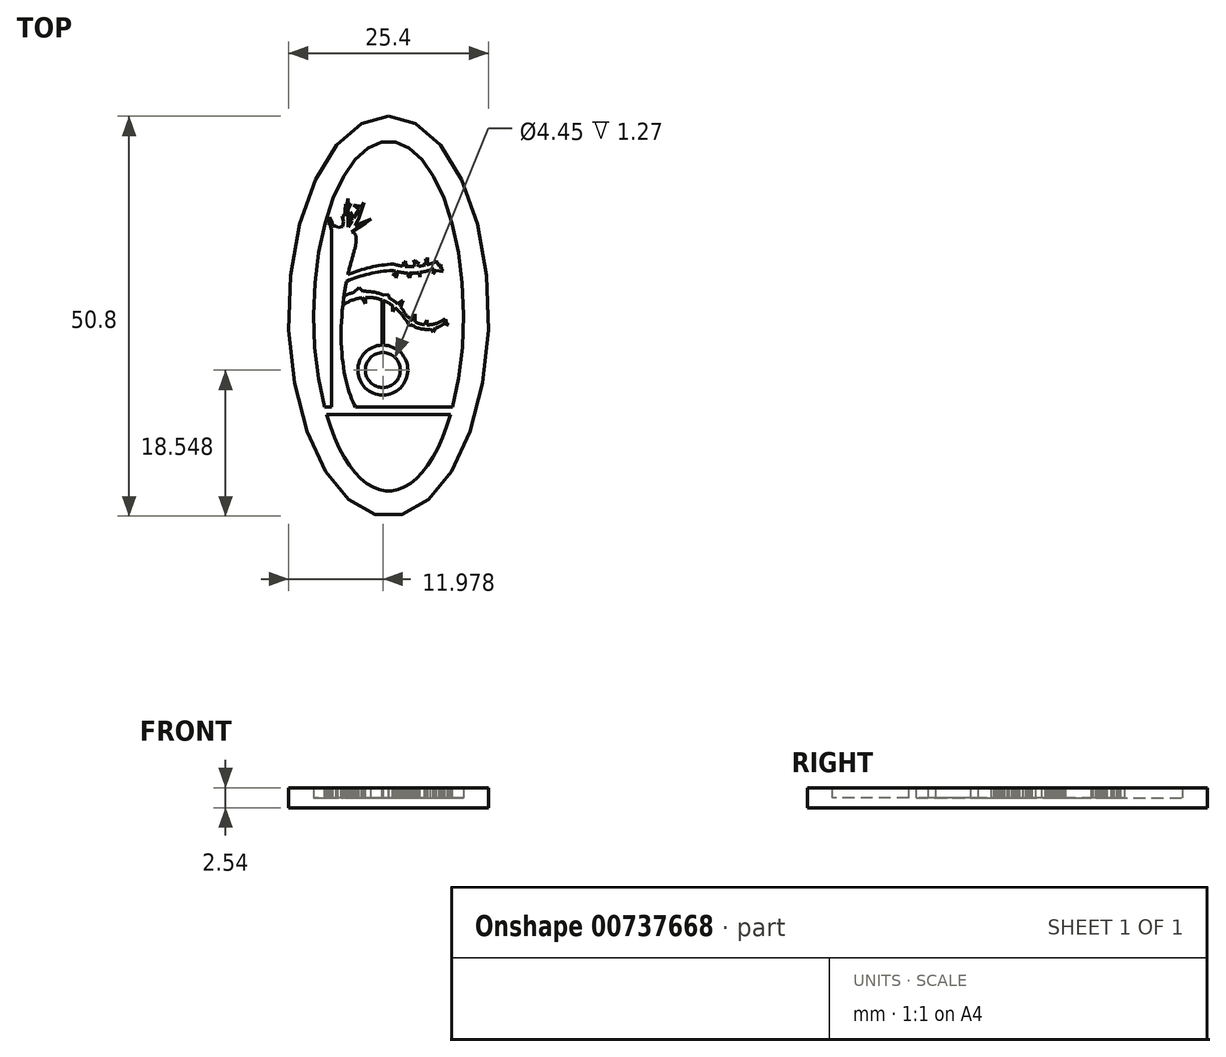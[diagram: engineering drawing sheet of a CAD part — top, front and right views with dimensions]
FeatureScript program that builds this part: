
annotation { "Feature Type Name" : "Feature", "Feature Type Description" : "" }
export const myFeature = defineFeature(function(context is Context, id is Id, definition is map)
    precondition{}
    {
        {
            var Q0;
            Q0=qCreatedBy(makeId("Top.planeOp"),FACE);
            var sketch = newSketch(context, id + "F0", { "sketchPlane" : qUnion([Q0])});
            skEllipse(sketch, "E0", {"center": v(0, 0) * mm, "majorRadius": 25.4 * mm, "minorRadius": 12.7 * mm, "majorAxis": v(0, 1)});
            skSolve(sketch);
        }
        {
            var Q0;
            Q0=qSketchRegion(id+"F0",true);
            extrude(context, id + "F1", {"entities" : qUnion([Q0]), "depth" : 2.54 * mm, "offsetDistance" : 25.4 * mm});
        }
        {
            var Q0;
            Q0=makeQuery(id+"F1.opExtrude","CAP_FACE",FACE,{"disambiguationData":[OSD([sQuery(id+"F0.wireOp",EDGE,"E0")])],"isStart":false});
            var sketch = newSketch(context, id + "F2", { "sketchPlane" : qUnion([Q0])});
            skEllipse(sketch, "E1", {"center": v(0, 0) * mm, "majorRadius": 22.23 * mm, "minorRadius": 9.53 * mm, "majorAxis": v(0, 1)});
            skSolve(sketch);
        }
        {
            var Q0;
            Q0=qSketchRegion(id+"F2",true);
            extrude(context, id + "F3", {"entities" : qUnion([Q0]), "operationType" : NewBodyOperationType.REMOVE, "oppositeDirection" : true, "depth" : 1.27 * mm, "offsetDistance" : 25.4 * mm});
        }
        {
            var Q0;
            Q0=makeQuery(id+"F2.imprint","IMPRINT",FACE,{"disambiguationData":[TD([[makeQuery(id+"F2.imprint","IMPRINT",EDGE,{"derivedFrom":sQuery(id+"F2.wireOp",EDGE,"E1")}),1.0]])]});
            var sketch = newSketch(context, id + "F4", { "sketchPlane" : qUnion([Q0])});
            skLineSegment(sketch, "E2", {"start": v(-7.24, 10.97) * mm, "end": v(-7.24, -11.57) * mm});
            skLineSegment(sketch, "E3", {"start": v(-7.24, -11.57) * mm, "end": v(-4.19, -11.57) * mm});
            skFitSpline(sketch, "E4", {"points": [v(-4.19, -11.57) * mm, v(-5.86, -5.45) * mm, v(-5, 5.96) * mm, v(-4.49, 10.63) * mm, v(-7.24, 10.97) * mm], "startDerivative": vector(-8.15, 15.39) * mm, "endDerivative": vector(-7.13, 8.4) * mm});
            skArc(sketch, "E5", {"start": v(0.52, 5.8) * mm, "mid": v(-2.54, 5.35) * mm, "end": v(-5.48, 4.37) * mm});
            skArc(sketch, "E6", {"start": v(0.52, 5.8) * mm, "mid": v(3.17, 5.47) * mm, "end": v(5.77, 6.03) * mm});
            skArc(sketch, "E7", {"start": v(1.81, 0.02) * mm, "mid": v(-1.7, 2.3) * mm, "end": v(-5.8, 1.4) * mm});
            skArc(sketch, "E8", {"start": v(1.81, 0.02) * mm, "mid": v(4.23, -1.63) * mm, "end": v(7.07, -0.95) * mm});
            skLineSegment(sketch, "E9", {"start": v(-5.8, -18.4) * mm, "end": v(-5.71, -17.72) * mm});
            skArc(sketch, "E10", {"start": v(1.81, 0.83) * mm, "mid": v(-1.62, 3) * mm, "end": v(-5.66, 2.57) * mm});
            skArc(sketch, "E11", {"start": v(1.81, 0.83) * mm, "mid": v(4.1, -1) * mm, "end": v(6.97, -0.45) * mm});
            skLineSegment(sketch, "E12", {"start": v(7.6, -1.1) * mm, "end": v(7.07, -0.95) * mm});
            skLineSegment(sketch, "E13", {"start": v(7.6, -1.1) * mm, "end": v(6.99, -0.77) * mm});
            skLineSegment(sketch, "E14", {"start": v(6.99, -0.77) * mm, "end": v(7.47, -0.63) * mm});
            skLineSegment(sketch, "E15", {"start": v(7.47, -0.63) * mm, "end": v(7.07, -0.63) * mm});
            skLineSegment(sketch, "E16", {"start": v(7.07, -0.63) * mm, "end": v(7.15, -0.33) * mm});
            skLineSegment(sketch, "E17", {"start": v(7.15, -0.33) * mm, "end": v(6.97, -0.45) * mm});
            skArc(sketch, "E18", {"start": v(0.6, 6.62) * mm, "mid": v(-2.46, 6.17) * mm, "end": v(-5.4, 5.18) * mm});
            skArc(sketch, "E19", {"start": v(0.6, 6.62) * mm, "mid": v(3.25, 6.28) * mm, "end": v(5.85, 6.84) * mm});
            skLineSegment(sketch, "E20", {"start": v(5.77, 6.03) * mm, "end": v(5.68, 5.38) * mm});
            skLineSegment(sketch, "E21", {"start": v(5.68, 5.38) * mm, "end": v(6.04, 5.78) * mm});
            skLineSegment(sketch, "E22", {"start": v(6.04, 5.78) * mm, "end": v(6.93, 5.66) * mm});
            skLineSegment(sketch, "E23", {"start": v(6.93, 5.66) * mm, "end": v(6.77, 5.83) * mm});
            skLineSegment(sketch, "E24", {"start": v(6.77, 5.83) * mm, "end": v(6.94, 6.03) * mm});
            skLineSegment(sketch, "E25", {"start": v(6.94, 6.03) * mm, "end": v(6.62, 6.05) * mm});
            skLineSegment(sketch, "E26", {"start": v(6.62, 6.05) * mm, "end": v(6.66, 6.57) * mm});
            skLineSegment(sketch, "E27", {"start": v(6.66, 6.57) * mm, "end": v(6.43, 6.3) * mm});
            skLineSegment(sketch, "E28", {"start": v(6.43, 6.3) * mm, "end": v(6.43, 6.69) * mm});
            skLineSegment(sketch, "E29", {"start": v(6.43, 6.69) * mm, "end": v(6.07, 6.7) * mm});
            skLineSegment(sketch, "E30", {"start": v(6.07, 6.7) * mm, "end": v(6.07, 7.1) * mm});
            skLineSegment(sketch, "E31", {"start": v(6.07, 7.1) * mm, "end": v(5.85, 6.84) * mm});
            skPoint(sketch, "E32.endSnap0", {"position": v(-2.24, 12.35) * mm});
            skLineSegment(sketch, "E33", {"start": v(-3.78, 12.35) * mm, "end": v(-3.13, 14.44) * mm});
            skLineSegment(sketch, "E34", {"start": v(-3.13, 14.44) * mm, "end": v(-5.16, 11.35) * mm});
            skLineSegment(sketch, "E35", {"start": v(-5.16, 11.35) * mm, "end": v(-5.16, 14.91) * mm});
            skLineSegment(sketch, "E36", {"start": v(-7.67, 12.4) * mm, "end": v(-7.24, 10.97) * mm});
            skLineSegment(sketch, "E37", {"start": v(-2.93, 11.82) * mm, "end": v(-2.76, 10.93) * mm});
            skLineSegment(sketch, "E38", {"start": v(-2.76, 10.93) * mm, "end": v(-3.1, 11.69) * mm});
            skLineSegment(sketch, "E39", {"start": v(-4.63, 12.14) * mm, "end": v(-4.9, 13.23) * mm});
            skLineSegment(sketch, "E40", {"start": v(-4.9, 13.23) * mm, "end": v(-4.44, 12.44) * mm});
            skLineSegment(sketch, "E41", {"start": v(-4.44, 12.44) * mm, "end": v(-3.72, 13.55) * mm});
            skLineSegment(sketch, "E42", {"start": v(-3.72, 13.55) * mm, "end": v(-4.44, 14.13) * mm});
            skLineSegment(sketch, "E43", {"start": v(-4.44, 14.13) * mm, "end": v(-3.46, 13.95) * mm});
            skLineSegment(sketch, "E44", {"start": v(-5.16, 13.61) * mm, "end": v(-4.75, 14.27) * mm});
            skLineSegment(sketch, "E45", {"start": v(-4.75, 14.27) * mm, "end": v(-5.16, 13.98) * mm});
            skLineSegment(sketch, "E46", {"start": v(-7.01, 11.42) * mm, "end": v(-7.25, 12.06) * mm});
            skLineSegment(sketch, "E47", {"start": v(-7.25, 12.06) * mm, "end": v(-7.46, 12.6) * mm});
            skLineSegment(sketch, "E48", {"start": v(-7.46, 12.6) * mm, "end": v(-7.46, 12.23) * mm});
            skLineSegment(sketch, "E49", {"start": v(-7.46, 12.23) * mm, "end": v(-7.5, 11.84) * mm});
            skLineSegment(sketch, "E50", {"start": v(-7.5, 11.84) * mm, "end": v(-7.7, 11.86) * mm});
            skLineSegment(sketch, "E51", {"start": v(-7.7, 11.86) * mm, "end": v(-7.44, 11.65) * mm});
            skLineSegment(sketch, "E52", {"start": v(4.9, 6.53) * mm, "end": v(4.99, 7.45) * mm});
            skLineSegment(sketch, "E53", {"start": v(4.99, 7.45) * mm, "end": v(4.62, 6.46) * mm});
            skLineSegment(sketch, "E54", {"start": v(4.62, 6.46) * mm, "end": v(3.79, 6.33) * mm});
            skLineSegment(sketch, "E55", {"start": v(3.79, 6.33) * mm, "end": v(3.37, 7.16) * mm});
            skLineSegment(sketch, "E56", {"start": v(3.37, 7.16) * mm, "end": v(3.25, 6.28) * mm});
            skLineSegment(sketch, "E57", {"start": v(3.25, 6.28) * mm, "end": v(2.1, 6.32) * mm});
            skLineSegment(sketch, "E58", {"start": v(2.1, 6.32) * mm, "end": v(2.16, 7.01) * mm});
            skLineSegment(sketch, "E59", {"start": v(2.16, 7.01) * mm, "end": v(1.75, 6.36) * mm});
            skLineSegment(sketch, "E60", {"start": v(1.75, 6.36) * mm, "end": v(2.44, 5.47) * mm});
            skLineSegment(sketch, "E61", {"start": v(2.44, 5.47) * mm, "end": v(2.7, 4.86) * mm});
            skLineSegment(sketch, "E62", {"start": v(2.7, 4.86) * mm, "end": v(2.7, 5.47) * mm});
            skLineSegment(sketch, "E63", {"start": v(2.7, 5.47) * mm, "end": v(3.83, 5.53) * mm});
            skLineSegment(sketch, "E64", {"start": v(3.83, 5.53) * mm, "end": v(4.04, 4.94) * mm});
            skLineSegment(sketch, "E65", {"start": v(4.04, 4.94) * mm, "end": v(4.04, 5.56) * mm});
            skLineSegment(sketch, "E66", {"start": v(4.04, 5.56) * mm, "end": v(1.1, 5.65) * mm});
            skLineSegment(sketch, "E67", {"start": v(1.1, 5.65) * mm, "end": v(0.98, 4.83) * mm});
            skLineSegment(sketch, "E68", {"start": v(0.98, 4.83) * mm, "end": v(0.88, 5.7) * mm});
            skLineSegment(sketch, "E69", {"start": v(0.88, 5.7) * mm, "end": v(0.93, 5.27) * mm});
            skLineSegment(sketch, "E70", {"start": v(0.93, 5.27) * mm, "end": v(0.53, 5.32) * mm});
            skLineSegment(sketch, "E71", {"start": v(0.53, 5.32) * mm, "end": v(0.95, 5.03) * mm});
            skLineSegment(sketch, "E72", {"start": v(0.95, 5.03) * mm, "end": v(1.06, 5.36) * mm});
            skLineSegment(sketch, "E73", {"start": v(1.06, 5.36) * mm, "end": v(1.26, 5.33) * mm});
            skLineSegment(sketch, "E74", {"start": v(1.26, 5.33) * mm, "end": v(1.08, 5.52) * mm});
            skLineSegment(sketch, "E75", {"start": v(1.93, 6.65) * mm, "end": v(1.88, 6.87) * mm});
            skLineSegment(sketch, "E76", {"start": v(1.88, 6.87) * mm, "end": v(1.85, 6.52) * mm});
            skLineSegment(sketch, "E77", {"start": v(1.85, 6.52) * mm, "end": v(2.11, 6.52) * mm});
            skLineSegment(sketch, "E78", {"start": v(2.11, 6.52) * mm, "end": v(2.39, 6.6) * mm});
            skLineSegment(sketch, "E79", {"start": v(2.39, 6.6) * mm, "end": v(2.1, 6.42) * mm});
            skLineSegment(sketch, "E80", {"start": v(2.95, 5.1) * mm, "end": v(2.7, 5.3) * mm});
            skLineSegment(sketch, "E81", {"start": v(2.7, 5.3) * mm, "end": v(2.95, 5.1) * mm});
            skLineSegment(sketch, "E82", {"start": v(2.7, 5.1) * mm, "end": v(2.95, 5.1) * mm});
            skLineSegment(sketch, "E83", {"start": v(2.57, 5.17) * mm, "end": v(2.46, 4.95) * mm});
            skLineSegment(sketch, "E84", {"start": v(2.46, 4.95) * mm, "end": v(2.52, 5.27) * mm});
            skLineSegment(sketch, "E85", {"start": v(2.52, 5.27) * mm, "end": v(3.59, 6.72) * mm});
            skLineSegment(sketch, "E86", {"start": v(3.59, 6.72) * mm, "end": v(3.84, 6.91) * mm});
            skLineSegment(sketch, "E87", {"start": v(3.84, 6.91) * mm, "end": v(3.67, 6.56) * mm});
            skLineSegment(sketch, "E88", {"start": v(3.67, 6.56) * mm, "end": v(3.32, 6.82) * mm});
            skLineSegment(sketch, "E89", {"start": v(3.32, 6.82) * mm, "end": v(3.18, 7.1) * mm});
            skLineSegment(sketch, "E90", {"start": v(3.18, 7.1) * mm, "end": v(3.34, 6.98) * mm});
            skLineSegment(sketch, "E91", {"start": v(4.83, 7.04) * mm, "end": v(4.68, 7.29) * mm});
            skLineSegment(sketch, "E92", {"start": v(4.68, 7.29) * mm, "end": v(4.78, 6.9) * mm});
            skLineSegment(sketch, "E93", {"start": v(4.78, 6.9) * mm, "end": v(4.7, 6.67) * mm});
            skLineSegment(sketch, "E94", {"start": v(4.7, 6.67) * mm, "end": v(4.57, 6.82) * mm});
            skLineSegment(sketch, "E95", {"start": v(4.57, 6.82) * mm, "end": v(4.66, 6.57) * mm});
            skLineSegment(sketch, "E96", {"start": v(4.66, 6.57) * mm, "end": v(4.93, 6.87) * mm});
            skLineSegment(sketch, "E97", {"start": v(4.93, 6.87) * mm, "end": v(5.03, 6.78) * mm});
            skLineSegment(sketch, "E98", {"start": v(5.03, 6.78) * mm, "end": v(4.92, 6.78) * mm});
            skLineSegment(sketch, "E99", {"start": v(4.92, 6.78) * mm, "end": v(3.86, 5.44) * mm});
            skLineSegment(sketch, "E100", {"start": v(3.86, 5.44) * mm, "end": v(3.78, 5.22) * mm});
            skLineSegment(sketch, "E101", {"start": v(3.78, 5.22) * mm, "end": v(3.92, 5.27) * mm});
            skLineSegment(sketch, "E102", {"start": v(-4.44, 3) * mm, "end": v(-3.73, 3.66) * mm});
            skLineSegment(sketch, "E103", {"start": v(-3.73, 3.66) * mm, "end": v(-3.26, 3.16) * mm});
            skLineSegment(sketch, "E104", {"start": v(-3.26, 3.16) * mm, "end": v(-3.26, 3.16) * mm});
            skLineSegment(sketch, "E105", {"start": v(-2.92, 2.38) * mm, "end": v(-2.92, 1.62) * mm});
            skLineSegment(sketch, "E106", {"start": v(-2.92, 1.62) * mm, "end": v(-3.38, 2.34) * mm});
            skLineSegment(sketch, "E107", {"start": v(-0.65, 2.69) * mm, "end": v(0, 2.77) * mm});
            skLineSegment(sketch, "E108", {"start": v(0.5, 1.37) * mm, "end": v(0.5, 0.6) * mm});
            skLineSegment(sketch, "E109", {"start": v(0.5, 0.6) * mm, "end": v(0.82, 1.11) * mm});
            skLineSegment(sketch, "E110", {"start": v(1.84, 1.97) * mm, "end": v(1.55, 1.14) * mm});
            skLineSegment(sketch, "E111", {"start": v(2.28, -0.57) * mm, "end": v(2.64, -1.3) * mm});
            skLineSegment(sketch, "E112", {"start": v(3.37, 0.24) * mm, "end": v(3.37, -0.74) * mm});
            skLineSegment(sketch, "E113", {"start": v(4.45, -1.28) * mm, "end": v(4.86, -0.46) * mm});
            skLineSegment(sketch, "E114", {"start": v(4.86, -0.46) * mm, "end": v(4.86, -1.1) * mm});
            skLineSegment(sketch, "E115", {"start": v(4.86, -1.1) * mm, "end": v(5.66, -2.04) * mm});
            skLineSegment(sketch, "E116", {"start": v(5.66, -2.04) * mm, "end": v(5.96, -1.52) * mm});
            skLineSegment(sketch, "E117", {"start": v(1.84, 1.97) * mm, "end": v(1.13, 1.56) * mm});
            skPoint(sketch, "E117.endSnap0", {"position": v(1.7, 1.56) * mm});
            skLineSegment(sketch, "E118", {"start": v(0, 2.77) * mm, "end": v(0.05, 2.34) * mm});
            skLineSegment(sketch, "E119", {"start": v(3.37, 0.24) * mm, "end": v(3.04, -0.55) * mm});
            skLineSegment(sketch, "E120", {"start": v(3.04, -0.55) * mm, "end": v(3.37, 0.24) * mm});
            skLineSegment(sketch, "E121", {"start": v(2.64, -1.3) * mm, "end": v(2.79, -1.02) * mm});
            skLineSegment(sketch, "E122", {"start": v(1.81, 0.02) * mm, "end": v(1.81, 0.83) * mm});
            skLineSegment(sketch, "E123", {"start": v(-8.52, -11.57) * mm, "end": v(8.47, -11.57) * mm});
            skLineSegment(sketch, "E124", {"start": v(-8.52, -11.57) * mm, "end": v(-8.19, -12.52) * mm});
            skLineSegment(sketch, "E125", {"start": v(-8.19, -12.52) * mm, "end": v(8.37, -12.52) * mm});
            skLineSegment(sketch, "E126", {"start": v(8.37, -12.52) * mm, "end": v(8.47, -11.57) * mm});
            skPoint(sketch, "E127", {"position": v(-5.8, 1.4) * mm});
            skLineSegment(sketch, "E128", {"start": v(-5.66, 2.57) * mm, "end": v(-5.8, 1.4) * mm});
            skLineSegment(sketch, "E129", {"start": v(-0.65, 2) * mm, "end": v(-0.65, -3.68) * mm});
            skLineSegment(sketch, "E130", {"start": v(-0.65, -3.68) * mm, "end": v(-0.8, -3.68) * mm});
            skLineSegment(sketch, "E131", {"start": v(-0.8, -3.68) * mm, "end": v(-0.8, 2.05) * mm});
            skCircle(sketch, "E132", {"center": v(-0.72, -6.85) * mm, "radius": 3.18 * mm});
            skPoint(sketch, "E132.third.point", {"position": v(0.58, -9.75) * mm});
            skCircle(sketch, "E133", {"center": v(-0.72, -6.85) * mm, "radius": 2.22 * mm});
            skLineSegment(sketch, "E134", {"start": v(-7.67, 12.4) * mm, "end": v(-7.46, 12.23) * mm});
            skLineSegment(sketch, "E135", {"start": v(-5.16, 14.91) * mm, "end": v(-5.86, 11.38) * mm});
            skLineSegment(sketch, "E136", {"start": v(-5.86, 11.38) * mm, "end": v(-6.43, 11.26) * mm});
            skLineSegment(sketch, "E137", {"start": v(-6.43, 11.26) * mm, "end": v(-6.67, 11.47) * mm});
            skLineSegment(sketch, "E138", {"start": v(-6.67, 11.47) * mm, "end": v(-7.01, 11.42) * mm});
            skLineSegment(sketch, "E139", {"start": v(-5.48, 13.3) * mm, "end": v(-5.48, 14.23) * mm});
            skLineSegment(sketch, "E140", {"start": v(-5.48, 14.23) * mm, "end": v(-5.6, 12.69) * mm});
            skLineSegment(sketch, "E141", {"start": v(-5.6, 12.69) * mm, "end": v(-5.88, 12.74) * mm});
            skLineSegment(sketch, "E142", {"start": v(-5.88, 12.74) * mm, "end": v(-5.74, 12) * mm});
            skLineSegment(sketch, "E143", {"start": v(-2.93, 11.82) * mm, "end": v(-2.93, 11.82) * mm});
            skLineSegment(sketch, "E144", {"start": v(-2.93, 11.82) * mm, "end": v(-4.7, 10.71) * mm});
            skLineSegment(sketch, "E145", {"start": v(-4.7, 10.71) * mm, "end": v(-3.78, 12.35) * mm});
            skLineSegment(sketch, "E146", {"start": v(-2.93, 11.82) * mm, "end": v(-2.24, 12.35) * mm});
            skLineSegment(sketch, "E147", {"start": v(-2.24, 12.35) * mm, "end": v(-4.24, 11.53) * mm});
            skLineSegment(sketch, "E148", {"start": v(-4.11, 9.55) * mm, "end": v(0.67, 11.42) * mm});
            skLineSegment(sketch, "E149", {"start": v(-4.2, 9) * mm, "end": v(0.84, 10.95) * mm});
            skSolve(sketch);
        }
        {
            var Q0;
            Q0 = qSketchRegion(id + "F4", true);
            extrude(context, id + "F5", {"entities" : qUnion([Q0]), "operationType" : NewBodyOperationType.ADD, "oppositeDirection" : true, "depth" : 1.52 * mm, "offsetDistance" : 25.4 * mm});
        }
    });
